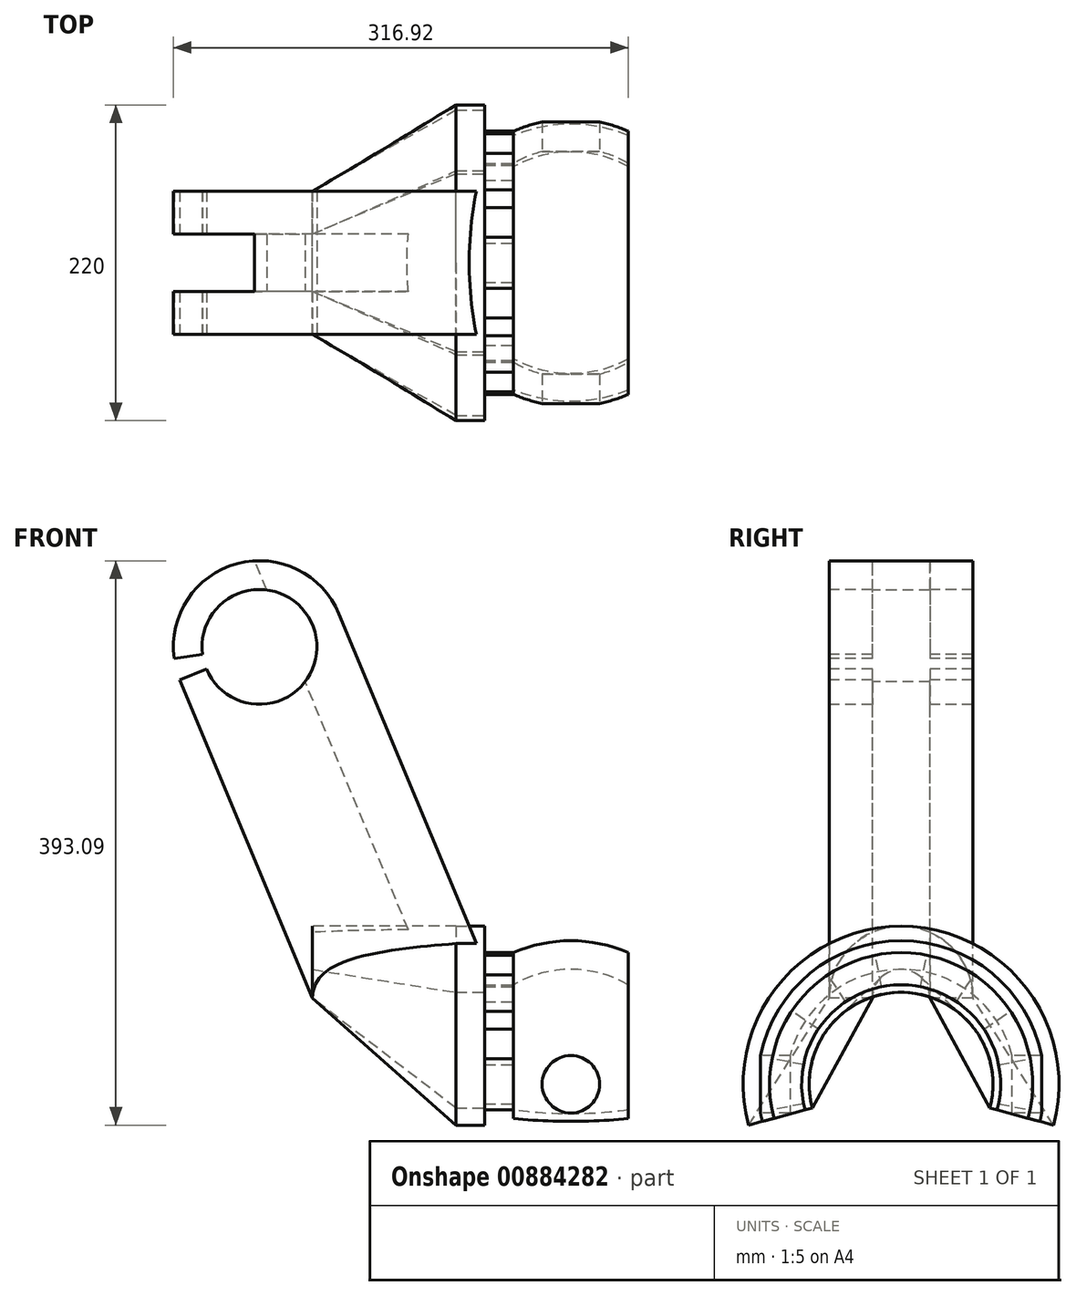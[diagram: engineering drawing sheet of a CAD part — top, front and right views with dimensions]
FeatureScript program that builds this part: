
annotation { "Feature Type Name" : "Feature", "Feature Type Description" : "" }
export const myFeature = defineFeature(function(context is Context, id is Id, definition is map)
    precondition{}
    {
        {
            var Q0;
            Q0=qCreatedBy(makeId("Front.planeOp"),FACE);
            var sketch = newSketch(context, id + "F0", { "sketchPlane" : qUnion([Q0])});
            skLineSegment(sketch, "E0", {"start": v(0, 0) * mm, "end": v(154.67, 0) * mm, "construction": true});
            skLineSegment(sketch, "E1", {"start": v(40, 91.65) * mm, "end": v(40, 69.28) * mm});
            skLineSegment(sketch, "E2", {"start": v(-40, 91.65) * mm, "end": v(-40, 69.28) * mm});
            skArc(sketch, "E3", {"start": v(40, 69.28) * mm, "mid": v(0, 80) * mm, "end": v(-40, 69.28) * mm});
            skLineSegment(sketch, "E4", {"start": v(0, 2.73) * mm, "end": v(0, 112.94) * mm, "construction": true});
            skArc(sketch, "E5", {"start": v(40, 91.65) * mm, "mid": v(0, 100) * mm, "end": v(-40, 91.65) * mm});
            skSolve(sketch);
        }
        {
            var Q0;
            Q0=makeQuery(id+"F0.imprint","IMPRINT",FACE,{"disambiguationData":[TD([[makeQuery(id+"F0.imprint","IMPRINT",EDGE,{"derivedFrom":sQuery(id+"F0.wireOp",EDGE,"E1")}),-1.0]])]});
            var Q1;
            Q1=sQuery(id+"F0.wireOp",EDGE,"E0");
            revolve(context, id + "F1", {"surfaceOperationType" : NewSurfaceOperationType.NEW, "entities" : qUnion([Q0]), "axis" : qUnion([Q1]), "revolveType" : RevolveType.SYMMETRIC, "angle" : 210 * degree});
        }
        {
            var Q0;
            Q0=qCreatedBy(makeId("Front.planeOp"),FACE);
            var sketch = newSketch(context, id + "F2", { "sketchPlane" : qUnion([Q0])});
            skCircle(sketch, "E6", {"center": v(0, 0) * mm, "radius": 20 * mm});
            skSolve(sketch);
        }
        {
            var Q0;
            Q0=qSketchRegion(id+"F2",true);
            extrude(context, id + "F3", {"entities" : qUnion([Q0]), "operationType" : NewBodyOperationType.REMOVE, "endBound" : BoundingType.THROUGH_ALL, "oppositeDirection" : true, "depth" : 25 * mm, "offsetDistance" : 25 * mm, "hasSecondDirection" : true, "secondDirectionBound" : SecondDirectionBoundingType.THROUGH_ALL, "secondDirectionOppositeDirection" : false, "secondDirectionDepth" : 25 * mm});
        }
        {
            var Q0;
            Q0=makeQuery(id+"F1.opRevolve","SWEPT_FACE",FACE,{"disambiguationData":[OSD([sQuery(id+"F0.wireOp",EDGE,"E2")])]});
            var sketch = newSketch(context, id + "F4", { "sketchPlane" : qUnion([Q0])});
            skLineSegment(sketch, "E7", {"start": v(0, 69.28) * mm, "end": v(0, 91.65) * mm});
            skLineSegment(sketch, "E8.1.0", {"start": v(-13.52, 67.95) * mm, "end": v(-17.88, 89.9) * mm});
            skLineSegment(sketch, "E8.3.0", {"start": v(-38.5, 57.6) * mm, "end": v(-50.92, 76.2) * mm});
            skLineSegment(sketch, "E8.5.0", {"start": v(-57.6, 38.5) * mm, "end": v(-76.2, 50.92) * mm});
            skLineSegment(sketch, "E8.7.0", {"start": v(-67.95, 13.52) * mm, "end": v(-89.9, 17.88) * mm});
            skLineSegment(sketch, "E8.9.0", {"start": v(-67.95, -13.52) * mm, "end": v(-89.9, -17.88) * mm});
            skLineSegment(sketch, "E8.23.0", {"start": v(67.95, -13.52) * mm, "end": v(89.9, -17.88) * mm});
            skLineSegment(sketch, "E8.25.0", {"start": v(67.95, 13.52) * mm, "end": v(89.9, 17.88) * mm});
            skLineSegment(sketch, "E8.27.0", {"start": v(57.6, 38.5) * mm, "end": v(76.2, 50.92) * mm});
            skLineSegment(sketch, "E8.29.0", {"start": v(38.5, 57.6) * mm, "end": v(50.92, 76.2) * mm});
            skLineSegment(sketch, "E8.31.0", {"start": v(13.52, 67.95) * mm, "end": v(17.88, 89.9) * mm});
            skPoint(sketch, "E8.center", {"position": v(0, 0) * mm});
            skArc(sketch, "E9", {"start": v(-38.5, 57.6) * mm, "mid": v(-48.99, 48.99) * mm, "end": v(-57.6, 38.5) * mm});
            skArc(sketch, "E10", {"start": v(-50.92, 76.2) * mm, "mid": v(-64.8, 64.8) * mm, "end": v(-76.2, 50.92) * mm});
            skArc(sketch, "E11.trimOffspring", {"start": v(-67.95, 13.52) * mm, "mid": v(-69.28, 0) * mm, "end": v(-67.95, -13.52) * mm});
            skArc(sketch, "E12.trimOffspring", {"start": v(-89.9, 17.88) * mm, "mid": v(-91.65, 0) * mm, "end": v(-89.9, -17.88) * mm});
            skArc(sketch, "E13.trimOffspring", {"start": v(89.9, -17.88) * mm, "mid": v(91.65, 0) * mm, "end": v(89.9, 17.88) * mm});
            skArc(sketch, "E14.trimOffspring", {"start": v(67.95, -13.52) * mm, "mid": v(68.95, -6.8) * mm, "end": v(69.28, 0) * mm});
            skArc(sketch, "E15.trimOffspring", {"start": v(76.2, 50.92) * mm, "mid": v(64.8, 64.8) * mm, "end": v(50.92, 76.2) * mm});
            skArc(sketch, "E16.trimOffspring", {"start": v(57.6, 38.5) * mm, "mid": v(48.99, 48.99) * mm, "end": v(38.5, 57.6) * mm});
            skArc(sketch, "E17.trimOffspring", {"start": v(13.52, 67.95) * mm, "mid": v(0, 69.28) * mm, "end": v(-13.52, 67.95) * mm});
            skArc(sketch, "E18.trimOffspring", {"start": v(17.88, 89.9) * mm, "mid": v(0, 91.65) * mm, "end": v(-17.88, 89.9) * mm});
            skSolve(sketch);
        }
        {
            var Q0;
            {var subQ0=sQuery(id+"F4.wireOp",EDGE,"E7");Q0=makeQuery(id+"F4.imprint","IMPRINT",FACE,{"disambiguationData":[TD([[makeQuery(id+"F4.imprint","IMPRINT",EDGE,{"derivedFrom":subQ0}),-1.0]])]});}
            var Q1;
            Q1=makeQuery(id+"F4.imprint","IMPRINT",FACE,{"disambiguationData":[TD([[makeQuery(id+"F4.imprint","IMPRINT",EDGE,{"derivedFrom":sQuery(id+"F4.wireOp",EDGE,"E8.3.0")}),1.0]])]});
            var Q2;
            Q2=makeQuery(id+"F4.imprint","IMPRINT",FACE,{"disambiguationData":[TD([[makeQuery(id+"F4.imprint","IMPRINT",EDGE,{"derivedFrom":sQuery(id+"F4.wireOp",EDGE,"E8.7.0")}),1.0]])]});
            var Q3;
            Q3=makeQuery(id+"F4.imprint","IMPRINT",FACE,{"disambiguationData":[TD([[makeQuery(id+"F4.imprint","IMPRINT",EDGE,{"derivedFrom":sQuery(id+"F4.wireOp",EDGE,"E8.11.0")}),1.0]])]});
            var Q4;
            Q4=makeQuery(id+"F4.imprint","IMPRINT",FACE,{"disambiguationData":[TD([[makeQuery(id+"F4.imprint","IMPRINT",EDGE,{"derivedFrom":sQuery(id+"F4.wireOp",EDGE,"E8.15.0")}),1.0]])]});
            var Q5;
            Q5=makeQuery(id+"F4.imprint","IMPRINT",FACE,{"disambiguationData":[TD([[makeQuery(id+"F4.imprint","IMPRINT",EDGE,{"derivedFrom":sQuery(id+"F4.wireOp",EDGE,"E8.19.0")}),1.0]])]});
            var Q6;
            Q6=makeQuery(id+"F4.imprint","IMPRINT",FACE,{"disambiguationData":[TD([[makeQuery(id+"F4.imprint","IMPRINT",EDGE,{"derivedFrom":sQuery(id+"F4.wireOp",EDGE,"E8.27.0")}),1.0]])]});
            var Q7;
            {var subQ0=sQuery(id+"F4.wireOp",EDGE,"E7");Q7=makeQuery(id+"F4.imprint","IMPRINT",FACE,{"disambiguationData":[TD([[makeQuery(id+"F4.imprint","IMPRINT",EDGE,{"derivedFrom":subQ0}),1.0]])]});}
            var Q8;
            Q8=makeQuery(id+"F4.imprint","IMPRINT",FACE,{"disambiguationData":[TD([[makeQuery(id+"F4.imprint","IMPRINT",EDGE,{"derivedFrom":sQuery(id+"F4.wireOp",EDGE,"E8.23.0")}),1.0]])]});
            extrude(context, id + "F5", {"entities" : qUnion([Q0, Q1, Q2, Q3, Q4, Q5, Q6, Q7, Q8]), "operationType" : NewBodyOperationType.ADD, "depth" : 20 * mm, "offsetDistance" : 25 * mm});
        }
        {
            var Q0;
            Q0=makeQuery(id+"F5.opExtrude","CAP_FACE",FACE,{"disambiguationData":[OSD([sQuery(id+"F4.wireOp",EDGE,"E8.1.0"),sQuery(id+"F4.wireOp",EDGE,"E8.31.0"),sQuery(id+"F4.wireOp",EDGE,"E17.trimOffspring"),sQuery(id+"F4.wireOp",EDGE,"E18.trimOffspring")])],"isStart":false});
            var sketch = newSketch(context, id + "F6", { "sketchPlane" : qUnion([Q0])});
            skLineSegment(sketch, "E19", {"start": v(0, 0) * mm, "end": v(0, -196.2) * mm, "construction": true});
            skArc(sketch, "E20", {"start": v(106.25, -28.47) * mm, "mid": v(0, 110) * mm, "end": v(-106.25, -28.47) * mm});
            skArc(sketch, "E21", {"start": v(61.82, -16.56) * mm, "mid": v(0, 64) * mm, "end": v(-61.82, -16.56) * mm});
            skLineSegment(sketch, "E22", {"start": v(-61.82, -16.56) * mm, "end": v(-106.25, -28.47) * mm});
            skLineSegment(sketch, "E23.MirrorCS", {"start": v(61.82, -16.56) * mm, "end": v(106.25, -28.47) * mm});
            skSolve(sketch);
        }
        {
            var Q0;
            Q0=qSketchRegion(id+"F6",true);
            extrude(context, id + "F7", {"entities" : qUnion([Q0]), "operationType" : NewBodyOperationType.ADD, "depth" : 20 * mm, "offsetDistance" : 25 * mm});
        }
        {
            var Q0;
            Q0=makeQuery(id+"F7.opExtrude","CAP_FACE",FACE,{"disambiguationData":[OSD([sQuery(id+"F6.wireOp",EDGE,"E20"),sQuery(id+"F6.wireOp",EDGE,"E21"),sQuery(id+"F6.wireOp",EDGE,"E22"),sQuery(id+"F6.wireOp",EDGE,"E23.MirrorCS")])],"isStart":false});
            cPlane(context, id + "F8", {"entities" : qUnion([Q0]), "cplaneType" : CPlaneType.OFFSET, "offset" : 100 * mm, "width" : 150 * mm, "height" : 150 * mm});
        }
        {
            var Q0;
            Q0=qCreatedBy(id+"F8.planeOp",FACE);
            var sketch = newSketch(context, id + "F9", { "sketchPlane" : qUnion([Q0])});
            skArc(sketch, "E24", {"start": v(50, 60) * mm, "mid": v(0, 110) * mm, "end": v(-50, 60) * mm});
            skArc(sketch, "E25", {"start": v(20, 60) * mm, "mid": v(0, 80) * mm, "end": v(-20, 60) * mm});
            skLineSegment(sketch, "E26", {"start": v(-50, 60) * mm, "end": v(-20, 60) * mm});
            skLineSegment(sketch, "E27.trimOffspring", {"start": v(20, 60) * mm, "end": v(50, 60) * mm});
            skSolve(sketch);
        }
        {
            var Q0;
            Q0=qCreatedBy(makeId("Front.planeOp"),FACE);
            var sketch = newSketch(context, id + "F10", { "sketchPlane" : qUnion([Q0])});
            skLineSegment(sketch, "E28", {"start": v(-80, 110) * mm, "end": v(-180, 110) * mm});
            skSolve(sketch);
        }
        {
            var Q1;
            Q1=makeQuery(id+"F7.opExtrude","CAP_FACE",FACE,{"disambiguationData":[OSD([sQuery(id+"F6.wireOp",EDGE,"E20"),sQuery(id+"F6.wireOp",EDGE,"E21"),sQuery(id+"F6.wireOp",EDGE,"E22"),sQuery(id+"F6.wireOp",EDGE,"E23.MirrorCS")])],"isStart":false});
            var Q2;
            Q2=makeQuery(id+"F9.imprint","IMPRINT",FACE,{"disambiguationData":[TD([[makeQuery(id+"F9.imprint","IMPRINT",EDGE,{"derivedFrom":sQuery(id+"F9.wireOp",EDGE,"E24")}),1.0]])]});
            var Q3;
            Q3=sQuery(id+"F10.wireOp",EDGE,"E28");
            loft(context, id + "F11", {"operationType" : NewBodyOperationType.ADD, "addGuides" : true, "sheetProfilesArray" : [{ "sheetProfileEntities" : qUnion([Q1]) }, { "sheetProfileEntities" : qUnion([Q2]) }], "guidesArray" : [{ "guideEntities" : qUnion([Q3]), "guideDerivativeType" : LoftGuideDerivativeType.DEFAULT, "guideDerivativeMagnitude" : 1 }]});
        }
        {
            var Q0;
            Q0=sQuery(id+"F6.wireOp",EDGE,"E20");
            cPoint(context, id + "F12", {"entities" : qUnion([Q0]), "parameter" : 0.5});
        }
        {
            var Q0;
            Q0=makeQuery(id+"F11.opLoft","MID_CAP_VERTEX",VERTEX,{"disambiguationData":[OSD([sQuery(id+"F9.wireOp",EDGE,"E24"),sQuery(id+"F9.wireOp",EDGE,"E27.trimOffspring")])],"capPos":1.0});
            var Q1;
            Q1=makeQuery(id+"F11.opLoft","MID_CAP_VERTEX",VERTEX,{"disambiguationData":[OSD([sQuery(id+"F9.wireOp",EDGE,"E24"),sQuery(id+"F9.wireOp",EDGE,"E26")])],"capPos":1.0});
            var Q2;
            Q2 = qCreatedBy(id + "F12" ,VERTEX);
            cPlane(context, id + "F13", {"entities" : qUnion([Q0, Q1, Q2]), "cplaneType" : CPlaneType.THREE_POINT, "offset" : 25 * mm, "width" : 150 * mm, "height" : 150 * mm});
        }
        {
            var Q0;
            Q0=qCreatedBy(id+"F13.planeOp",FACE);
            var sketch = newSketch(context, id + "F14", { "sketchPlane" : qUnion([Q0])});
            skLineSegment(sketch, "E29", {"start": v(-143.08, -50) * mm, "end": v(-36.16, -50) * mm});
            skLineSegment(sketch, "E30", {"start": v(-36.16, -50) * mm, "end": v(-36.16, 50) * mm});
            skLineSegment(sketch, "E31", {"start": v(-36.16, 50) * mm, "end": v(-143.08, 50) * mm});
            skLineSegment(sketch, "E32", {"start": v(-143.08, 50) * mm, "end": v(-143.08, 20) * mm});
            skLineSegment(sketch, "E33", {"start": v(-143.08, 20) * mm, "end": v(-63.08, 20) * mm});
            skLineSegment(sketch, "E34", {"start": v(-63.08, 20) * mm, "end": v(-63.08, -20) * mm});
            skLineSegment(sketch, "E35", {"start": v(-63.08, -20) * mm, "end": v(-143.08, -20) * mm});
            skLineSegment(sketch, "E36", {"start": v(-143.08, -20) * mm, "end": v(-143.08, -50) * mm});
            skSolve(sketch);
        }
        {
            var Q0;
            Q0=qCreatedBy(id+"F13.planeOp",FACE);
            cPlane(context, id + "F15", {"entities" : qUnion([Q0]), "cplaneType" : CPlaneType.OFFSET, "offset" : 300 * mm, "width" : 150 * mm, "height" : 150 * mm});
        }
        {
            var Q0;
            Q0=qCreatedBy(id+"F15.planeOp",FACE);
            var sketch = newSketch(context, id + "F16", { "sketchPlane" : qUnion([Q0])});
            skLineSegment(sketch, "E37", {"start": v(-143.08, -50) * mm, "end": v(-23.08, -50) * mm});
            skLineSegment(sketch, "E38", {"start": v(-23.08, -50) * mm, "end": v(-23.08, 50) * mm});
            skLineSegment(sketch, "E39", {"start": v(-23.08, 50) * mm, "end": v(-143.08, 50) * mm});
            skLineSegment(sketch, "E40", {"start": v(-143.08, 50) * mm, "end": v(-143.08, 20) * mm});
            skLineSegment(sketch, "E41", {"start": v(-143.08, 20) * mm, "end": v(-63.08, 20) * mm});
            skLineSegment(sketch, "E42", {"start": v(-63.08, 20) * mm, "end": v(-63.08, -20) * mm});
            skLineSegment(sketch, "E43", {"start": v(-63.08, -20) * mm, "end": v(-143.08, -20) * mm});
            skLineSegment(sketch, "E44", {"start": v(-143.08, -20) * mm, "end": v(-143.08, -50) * mm});
            skSolve(sketch);
        }
        {
            var Q0;
            Q0=makeQuery(id+"F16.imprint","IMPRINT",FACE,{"disambiguationData":[TD([[makeQuery(id+"F16.imprint","IMPRINT",EDGE,{"derivedFrom":sQuery(id+"F16.wireOp",EDGE,"E37")}),1.0]])]});
            extrude(context, id + "F17", {"entities" : qUnion([Q0]), "endBound" : BoundingType.UP_TO_NEXT, "oppositeDirection" : true, "depth" : 25 * mm, "offsetDistance" : 25 * mm});
        }
        {
            var Q0;
            Q0=qCreatedBy(makeId("Front.planeOp"),FACE);
            var sketch = newSketch(context, id + "F18", { "sketchPlane" : qUnion([Q0])});
            skCircle(sketch, "E45", {"center": v(-216.92, 304.62) * mm, "radius": 40 * mm});
            skCircle(sketch, "E46", {"center": v(-216.92, 304.62) * mm, "radius": 60 * mm});
            skLineSegment(sketch, "E47", {"start": v(-161.54, 327.7) * mm, "end": v(-272.3, 281.54) * mm});
            skLineSegment(sketch, "E48", {"start": v(-216.92, 304.62) * mm, "end": v(-276.4, 296.66) * mm});
            skLineSegment(sketch, "E49", {"start": v(-161.54, 327.7) * mm, "end": v(-184.62, 383.08) * mm});
            skLineSegment(sketch, "E50", {"start": v(-184.62, 383.08) * mm, "end": v(-295.38, 336.92) * mm});
            skLineSegment(sketch, "E51", {"start": v(-295.38, 336.92) * mm, "end": v(-272.3, 281.54) * mm});
            skSolve(sketch);
        }
        {
            var Q0;
            {var subQ4=sQuery(id+"F18.wireOp",EDGE,"E51");Q0=makeQuery(id+"F18.imprint","IMPRINT",FACE,{"disambiguationData":[TD([[makeQuery(id+"F18.imprint","IMPRINT",EDGE,{"derivedFrom":subQ4}),1.0]])]});}
            var Q1;
            {var subQ0=sQuery(id+"F18.wireOp",EDGE,"E49");Q1=makeQuery(id+"F18.imprint","IMPRINT",FACE,{"disambiguationData":[TD([[makeQuery(id+"F18.imprint","IMPRINT",EDGE,{"derivedFrom":subQ0}),1.0]])]});}
            var Q2;
            {var subQ0=sQuery(id+"F18.wireOp",EDGE,"E48");var subQ1=sQuery(id+"F18.wireOp",EDGE,"E45");var subQ2=makeQuery(id+"F18.imprint","INTERSECT",VERTEX,{"derivedFrom":[subQ1,subQ0]});Q2=makeQuery(id+"F18.imprint","IMPRINT",FACE,{"disambiguationData":[TD([[makeQuery(id+"F18.imprint","IMPRINT",EDGE,{"disambiguationData":[TD([[subQ2,1.0]])],"derivedFrom":subQ1}),1.0]])]});}
            var Q3;
            {var subQ0=sQuery(id+"F18.wireOp",EDGE,"E48");var subQ1=sQuery(id+"F18.wireOp",EDGE,"E45");var subQ2=makeQuery(id+"F18.imprint","INTERSECT",VERTEX,{"derivedFrom":[subQ1,subQ0]});Q3=makeQuery(id+"F18.imprint","IMPRINT",FACE,{"disambiguationData":[TD([[makeQuery(id+"F18.imprint","IMPRINT",EDGE,{"disambiguationData":[TD([[subQ2,-1.0]])],"derivedFrom":subQ1}),1.0]])]});}
            var Q4;
            {var subQ0=sQuery(id+"F18.wireOp",EDGE,"E47");var subQ1=sQuery(id+"F18.wireOp",EDGE,"E45");var subQ2=makeQuery(id+"F18.imprint","INTERSECT",VERTEX,{"disambiguationData":[OD(0.0)],"derivedFrom":[subQ1,subQ0]});Q4=makeQuery(id+"F18.imprint","IMPRINT",FACE,{"disambiguationData":[TD([[makeQuery(id+"F18.imprint","IMPRINT",EDGE,{"disambiguationData":[TD([[subQ2,1.0]])],"derivedFrom":subQ1}),1.0]])]});}
            var Q5;
            {var subQ0=sQuery(id+"F18.wireOp",EDGE,"E48");var subQ1=sQuery(id+"F18.wireOp",EDGE,"E45");var subQ2=makeQuery(id+"F18.imprint","INTERSECT",VERTEX,{"derivedFrom":[subQ1,subQ0]});Q5=makeQuery(id+"F18.imprint","IMPRINT",FACE,{"disambiguationData":[TD([[makeQuery(id+"F18.imprint","IMPRINT",EDGE,{"disambiguationData":[TD([[subQ2,-1.0]])],"derivedFrom":subQ1}),-1.0]])]});}
            extrude(context, id + "F19", {"entities" : qUnion([Q0, Q1, Q2, Q3, Q4, Q5]), "operationType" : NewBodyOperationType.REMOVE, "endBound" : BoundingType.THROUGH_ALL, "oppositeDirection" : true, "depth" : 25 * mm, "offsetDistance" : 25 * mm, "hasSecondDirection" : true, "secondDirectionBound" : SecondDirectionBoundingType.THROUGH_ALL, "secondDirectionOppositeDirection" : false, "secondDirectionDepth" : 25 * mm});
        }
    });
